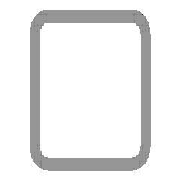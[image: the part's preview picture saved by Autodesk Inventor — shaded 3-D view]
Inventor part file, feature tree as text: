
AUTODESK INVENTOR PART (.ipt)
format: ipt  version: 2025.3 (Build 293356030, 356C)  size: 135,680 bytes
history: native  units: mm (DEFAULTED — no unit token found)
features: other x4, sketch x1, plane x1
ambient origin geometry x8: Origin, YZ Plane, XZ Plane, XY Plane, X Axis, Y Axis, Z Axis, Center Point
bodies: Solid1 (feature_tree), Body (feature_tree)
feature tree (6):
  parser-record x1  (decoder bookkeeping rows leaked as tree rows — omitted from the tree; the rows remain in map.json)
  other  "Driven Length"
  other  "Start Plane"
  other  "End Plane"
  sketch  "Sketch3"  dims[d3=450.0mm d4=0.0mm d7=4.0mm d9=40.0mm d11=40.0mm d12=2.0mm d13=40.0mm d14=490.0mm d15=20.0mm d16=20.0mm d17=90.0deg d18=450.0mm]
  plane  "Work Plane3"
